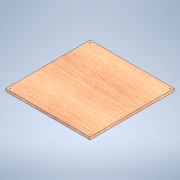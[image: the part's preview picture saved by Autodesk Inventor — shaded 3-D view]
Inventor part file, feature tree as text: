
AUTODESK INVENTOR PART (.ipt)
format: ipt  version: 2020 (Build 240168000, 168)  size: 130,560 bytes
history: native  units: mm
features: sketch x3, other x1, extrude x1, hole x1, projected_geometry x1
ambient origin geometry x8: Origin, YZ Plane, XZ Plane, XY Plane, X Axis, Y Axis, Z Axis, Center Point
bodies: Solid1 (feature_tree)
feature tree (7):
  other  "<userpath>\Documents\Development\paragon-printer\Paragon Printer Parameters.xlsx"
  sketch  "Sketch1"  dims[d0=400.0mm d1=400.0mm]
  extrude  "Extrusion1"  Depth=400.0mm
  hole  "Hole1"  [1 undecoded]
  sketch  "Sketch2"  dims[d2=12.7mm d3=0.0mm]
  sketch  "Sketch3"  dims[d4=10.0mm d5=3.4mm d6=6.0mm d7=6.3mm d8=2.0mm d9=90.0deg d10=8.0mm d11=20.594885mm]
  projected_geometry  "Projected Loop1"
note: 1 required parameter value undecoded (feature->parameter linkage not recoverable at this tier; creation-order binding heuristic only, values carry confidence <= 0.55)
